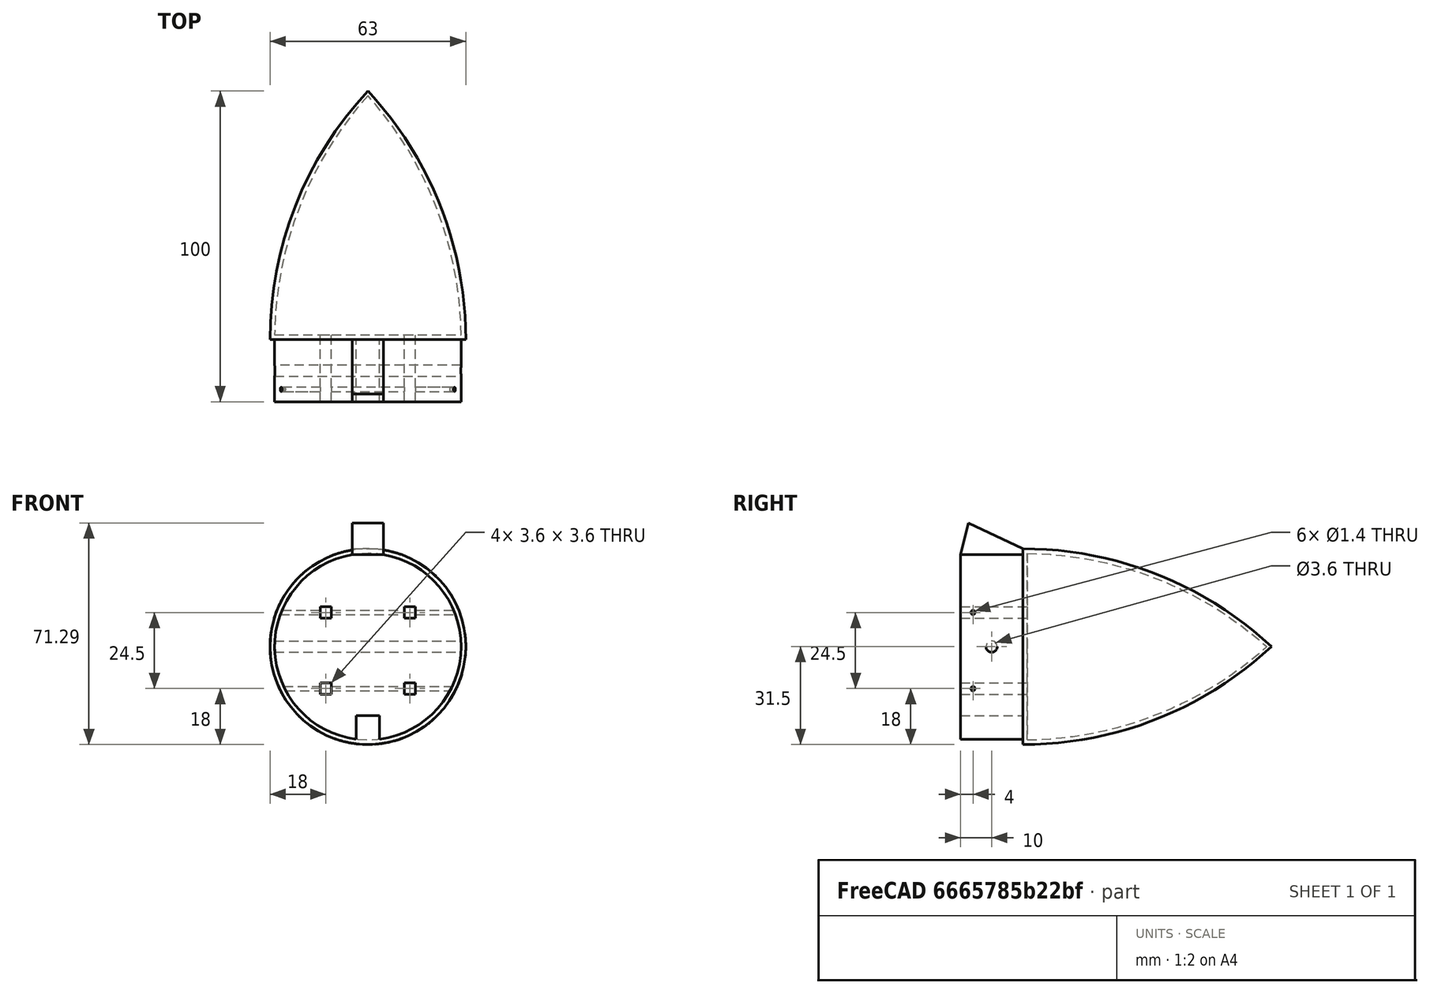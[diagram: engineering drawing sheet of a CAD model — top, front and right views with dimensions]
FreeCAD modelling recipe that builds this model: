
FCSTD DOCUMENT  (FreeCAD 1.0R38641 +468 (Git))
Label: ogive_cam-63_II
License: All rights reserved
LicenseURL: https://en.wikipedia.org/wiki/All_rights_reserved
objects: Sketcher::SketchObject×9, PartDesign::Pocket×6, PartDesign::Pad×2, PartDesign::Revolution×1, PartDesign::Mirrored×1, PartDesign::Body×1, Mesh::Feature×1
note: 48 computed .brp shape members not serialized (recipe doc carries the construction recipe); baked Part::Feature solids carry a one-line shape summary decoded from their .brp

FEATURE [Sketcher::SketchObject] Sketch
  ArcFitTolerance = 1e-06
  AttachmentSupport = -> [XY_Plane]
  FullyConstrained = false
  MakeInternals = false
  MapMode = 5
  sketch-geometry (6):
    g0: ArcOfCircle CenterX=85.695 CenterY=0.0560175 CenterZ=0 NormalX=0 NormalY=0 NormalZ=1 AngleXU=0 Radius=117.195 StartAngle=2.3909 EndAngle=3.14207
    g1: ArcOfCircle CenterX=87.6667 CenterY=0 CenterZ=0 NormalX=0 NormalY=0 NormalZ=1 AngleXU=0 Radius=117.676 StartAngle=2.4113 EndAngle=3.12885
    g2: LineSegment StartX=-1.42e-14 StartY=78.5 StartZ=0 EndX=1.42e-14 EndY=80 EndZ=0
    g3: LineSegment StartX=-30 StartY=1.5 StartZ=0 EndX=0 EndY=1.5 EndZ=0
    g4: LineSegment StartX=0 StartY=1.5 StartZ=0 EndX=0 EndY=0 EndZ=0
    g5: LineSegment StartX=0 StartY=0 StartZ=0 EndX=-31.5 EndY=0 EndZ=0
  constraints (18):
    c: PointOnObject(g0,g-2)
    c: DistanceY(g-1,g0) = 80
    c: PointOnObject(g1,g-1)
    c: PointOnObject(g1,g-2)
    c: Coincident(g2,g1)
    c: Coincident(g2,g0)
    c: Coincident(g1,g3)
    c: Coincident(g3,g4)
    c: Coincident(g4,g-1)
    c: Vertical(g4)
    c: Coincident(g4,g5)
    c: Coincident(g5,g0)
    c: Horizontal(g5)
    c: DistanceY(g2,g2) = 1.5
    c: DistanceY(g4,g4) = 1.5
    c: DistanceY(g4,g1) = 1.5
    c: DistanceX(g0,g1) = 1.5
    c: DistanceX(g0,g4) = 31.5
FEATURE [PartDesign::Revolution] Revolution
  Angle = 360
  Angle2 = 60
  Axis = (0,1,0)
  Base = (0,0,0)
  Profile = -> Sketch
  ReferenceAxis = -> Sketch [V_Axis]
  Refine = true
  Suppressed = false
  Type = 0
FEATURE [Sketcher::SketchObject] Sketch001
  ArcFitTolerance = 1e-06
  AttachmentSupport = -> [Revolution]
  FullyConstrained = true
  MakeInternals = false
  MapMode = 5
  Placement = pos=(0,0,0) rot=(1,0,0;1.5708rad)
  sketch-geometry (1):
    g0: Circle CenterX=0 CenterY=0 CenterZ=0 NormalX=0 NormalY=0 NormalZ=1 AngleXU=0 Radius=30
  constraints (2):
    c: Diameter(g0) = 60
    c: Coincident(g0,g-1)
FEATURE [PartDesign::Pad] Pad
  BaseFeature = -> Revolution
  Direction = (0,-1,2e-16)
  Length = 20
  Length2 = 10
  Profile = -> Sketch001
  ReferenceAxis = -> Sketch001 [N_Axis]
  Suppressed = false
  Type = 0
FEATURE [Sketcher::SketchObject] Sketch002
  ArcFitTolerance = 1e-06
  AttachmentSupport = -> [Pad]
  FullyConstrained = true
  MakeInternals = false
  MapMode = 5
  Placement = pos=(0,-20,4.4e-15) rot=(1,0,0;1.5708rad)
  sketch-geometry (4):
    g0: LineSegment StartX=-5 StartY=29 StartZ=0 EndX=5 EndY=29 EndZ=0
    g1: LineSegment StartX=5 StartY=29 StartZ=0 EndX=5 EndY=41 EndZ=0
    g2: LineSegment StartX=5 StartY=41 StartZ=0 EndX=-5 EndY=41 EndZ=0
    g3: LineSegment StartX=-5 StartY=41 StartZ=0 EndX=-5 EndY=29 EndZ=0
  constraints (11):
    c: Coincident(g0,g1)
    c: Coincident(g1,g2)
    c: Coincident(g2,g3)
    c: Coincident(g3,g0)
    c: Horizontal(g2)
    c: Vertical(g1)
    c: Vertical(g3)
    c: Distance(g1,g3) = 10
    c: Distance(g0,g2) = 12
    c: DistanceY(g-1,g0) = 29
    c: Symmetric(g0,g0,g-2)
FEATURE [PartDesign::Pad] Pad001
  BaseFeature = -> Pad
  Direction = (0,-1,2e-16)
  Length = 20
  Length2 = 10
  Profile = -> Sketch002
  ReferenceAxis = -> Sketch002 [N_Axis]
  Reversed = true
  Suppressed = false
  Type = 0
FEATURE [Sketcher::SketchObject] Sketch003
  ArcFitTolerance = 1e-06
  AttachmentSupport = -> [Pad001]
  ExternalGeometry = -> [Pad001]
  FullyConstrained = true
  MakeInternals = false
  MapMode = 5
  Placement = pos=(-5,0,0) rot=(0.57735,-0.57735,-0.57735;2.0944rad)
  sketch-geometry (3):
    g0: LineSegment StartX=20 StartY=41 StartZ=0 EndX=0 EndY=31.5 EndZ=0
    g1: LineSegment StartX=0 StartY=31.5 StartZ=0 EndX=0 EndY=41 EndZ=0
    g2: LineSegment StartX=0 StartY=41 StartZ=0 EndX=20 EndY=41 EndZ=0
  constraints (7):
    c: Coincident(g-4,g0)
    c: PointOnObject(g0,g-2)
    c: Coincident(g0,g1)
    c: Coincident(g1,g-4)
    c: Coincident(g1,g2)
    c: Coincident(g2,g0)
    c: DistanceY(g-1,g0) = 31.5
FEATURE [PartDesign::Pocket] Pocket
  BaseFeature = -> Pad001
  Direction = (1,0,0)
  Length = 5
  Length2 = 5
  Profile = -> Sketch003
  ReferenceAxis = -> Sketch003 [N_Axis]
  Suppressed = false
  Type = 1
FEATURE [Sketcher::SketchObject] Sketch004
  ArcFitTolerance = 1e-06
  AttachmentSupport = -> [Pocket]
  ExternalGeometry = -> [Pocket]
  FullyConstrained = false
  MakeInternals = false
  MapMode = 5
  Placement = pos=(-5,0,0) rot=(0.57735,-0.57735,-0.57735;2.0944rad)
  sketch-geometry (3):
    g0: LineSegment StartX=20 StartY=29.5804 StartZ=0 EndX=17.3381 EndY=40.211 EndZ=0
    g1: LineSegment StartX=17.3381 StartY=40.211 StartZ=0 EndX=20 EndY=41 EndZ=0
    g2: LineSegment StartX=20 StartY=41 StartZ=0 EndX=20 EndY=29.5804 EndZ=0
  constraints (5):
    c: Coincident(g-3,g0)
    c: Coincident(g0,g1)
    c: Coincident(g1,g-3)
    c: Coincident(g1,g2)
    c: Coincident(g2,g0)
FEATURE [PartDesign::Pocket] Pocket001
  BaseFeature = -> Pocket
  Direction = (1,0,0)
  Length = 5
  Length2 = 5
  Profile = -> Sketch004
  ReferenceAxis = -> Sketch004 [N_Axis]
  Suppressed = false
  Type = 1
FEATURE [Sketcher::SketchObject] Sketch005
  ArcFitTolerance = 1e-06
  AttachmentSupport = -> [Pocket001]
  FullyConstrained = true
  MakeInternals = false
  MapMode = 5
  Placement = pos=(0,-20,4.4e-15) rot=(1,0,0;1.5708rad)
  sketch-geometry (4):
    g0: LineSegment StartX=-3.7 StartY=-22.2 StartZ=0 EndX=-3.7 EndY=-30.2 EndZ=0
    g1: LineSegment StartX=-3.7 StartY=-30.2 StartZ=0 EndX=3.7 EndY=-30.2 EndZ=0
    g2: LineSegment StartX=3.7 StartY=-30.2 StartZ=0 EndX=3.7 EndY=-22.2 EndZ=0
    g3: LineSegment StartX=3.7 StartY=-22.2 StartZ=0 EndX=-3.7 EndY=-22.2 EndZ=0
  constraints (11):
    c: Coincident(g0,g1)
    c: Coincident(g1,g2)
    c: Coincident(g2,g3)
    c: Coincident(g3,g0)
    c: Vertical(g0)
    c: Vertical(g2)
    c: Horizontal(g1)
    c: DistanceY(g0,g0) = 8
    c: DistanceY(g0,g-1) = 22.2
    c: DistanceX(g3,g3) = 7.4
    c: Symmetric(g0,g2,g-2)
FEATURE [PartDesign::Pocket] Pocket002
  BaseFeature = -> Pocket001
  Direction = (0,1,-2e-16)
  Length = 20
  Length2 = 5
  Profile = -> Sketch005
  ReferenceAxis = -> Sketch005 [N_Axis]
  Suppressed = false
  Type = 0
FEATURE [Sketcher::SketchObject] Sketch006
  ArcFitTolerance = 1e-06
  AttachmentSupport = -> [Pocket002]
  FullyConstrained = true
  MakeInternals = false
  MapMode = 5
  Placement = pos=(0,-20,4.4e-15) rot=(1,0,0;1.5708rad)
  sketch-geometry (8):
    g0: LineSegment StartX=-15.3 StartY=12.8 StartZ=0 EndX=-15.3 EndY=9.2 EndZ=0
    g1: LineSegment StartX=-15.3 StartY=9.2 StartZ=0 EndX=-11.7 EndY=9.2 EndZ=0
    g2: LineSegment StartX=-11.7 StartY=9.2 StartZ=0 EndX=-11.7 EndY=12.8 EndZ=0
    g3: LineSegment StartX=-11.7 StartY=12.8 StartZ=0 EndX=-15.3 EndY=12.8 EndZ=0
    g4: LineSegment StartX=-15.3 StartY=-11.7 StartZ=0 EndX=-15.3 EndY=-15.3 EndZ=0
    g5: LineSegment StartX=-15.3 StartY=-15.3 StartZ=0 EndX=-11.7 EndY=-15.3 EndZ=0
    g6: LineSegment StartX=-11.7 StartY=-15.3 StartZ=0 EndX=-11.7 EndY=-11.7 EndZ=0
    g7: LineSegment StartX=-11.7 StartY=-11.7 StartZ=0 EndX=-15.3 EndY=-11.7 EndZ=0
  constraints (24):
    c: Coincident(g0,g1)
    c: Coincident(g1,g2)
    c: Coincident(g2,g3)
    c: Coincident(g3,g0)
    c: Vertical(g0)
    c: Vertical(g2)
    c: Horizontal(g1)
    c: Horizontal(g3)
    c: Distance(g0,g2) = 3.6
    c: Distance(g1,g3) = 3.6
    c: DistanceX(g1,g-1) = 11.7
    c: DistanceY(g-1,g1) = 9.2
    c: Coincident(g4,g5)
    c: Coincident(g5,g6)
    c: Coincident(g6,g7)
    c: Coincident(g7,g4)
    c: Vertical(g4)
    c: Vertical(g6)
    c: Horizontal(g5)
    c: Horizontal(g7)
    c: Distance(g4,g6) = 3.6
    c: Distance(g5,g7) = 3.6
    c: DistanceX(g6,g-1) = 11.7
    c: DistanceY(g6,g-1) = 11.7
FEATURE [PartDesign::Pocket] Pocket003
  BaseFeature = -> Pocket002
  Direction = (0,1,-2e-16)
  Length = 22
  Length2 = 5
  Profile = -> Sketch006
  ReferenceAxis = -> Sketch006 [N_Axis]
  Suppressed = false
  Type = 0
FEATURE [Sketcher::SketchObject] Sketch007
  ArcFitTolerance = 1e-06
  AttachmentSupport = -> [YZ_Plane]
  FullyConstrained = true
  MakeInternals = false
  MapMode = 5
  Placement = pos=(0,0,0) rot=(0.57735,0.57735,0.57735;2.0944rad)
  sketch-geometry (2):
    g0: Circle CenterX=-16 CenterY=-13.5 CenterZ=0 NormalX=0 NormalY=0 NormalZ=1 AngleXU=0 Radius=0.7
    g1: Circle CenterX=-16 CenterY=11 CenterZ=0 NormalX=0 NormalY=0 NormalZ=1 AngleXU=0 Radius=0.7
  constraints (6):
    c: Diameter(g0) = 1.4
    c: DistanceX(g0,g-1) = 16
    c: DistanceY(g0,g-1) = 13.5
    c: Diameter(g1) = 1.4
    c: DistanceX(g1,g-1) = 16
    c: DistanceY(g-1,g1) = 11
FEATURE [PartDesign::Pocket] Pocket004
  BaseFeature = -> Pocket003
  Direction = (-1,0,0)
  Length = 5
  Length2 = 5
  Midplane = true
  Profile = -> Sketch007
  ReferenceAxis = -> Sketch007 [N_Axis]
  Suppressed = false
  Type = 1
FEATURE [Sketcher::SketchObject] Sketch008
  ArcFitTolerance = 1e-06
  AttachmentSupport = -> [YZ_Plane]
  FullyConstrained = true
  MakeInternals = false
  MapMode = 5
  Placement = pos=(0,0,0) rot=(0.57735,0.57735,0.57735;2.0944rad)
  sketch-geometry (1):
    g0: Circle CenterX=-10 CenterY=0 CenterZ=0 NormalX=0 NormalY=0 NormalZ=1 AngleXU=0 Radius=1.8
  constraints (3):
    c: Diameter(g0) = 3.6
    c: PointOnObject(g0,g-1)
    c: DistanceX(g0,g-1) = 10
FEATURE [PartDesign::Pocket] Pocket005
  BaseFeature = -> Pocket004
  Direction = (-1,0,0)
  Length = 5
  Length2 = 5
  Midplane = true
  Profile = -> Sketch008
  ReferenceAxis = -> Sketch008 [N_Axis]
  Suppressed = false
  Type = 1
FEATURE [PartDesign::Mirrored] Mirrored001
  BaseFeature = -> Pocket005
  MirrorPlane = -> Sketch006 [V_Axis]
  Originals = -> [Pocket003]
  Suppressed = false
  TransformMode = 0
FEATURE [PartDesign::Body] Body  label="Corps"
  AllowCompound = false
  Group = -> [Sketch,Revolution,Sketch001,Pad,Sketch002,Pad001,Sketch003,Pocket,Sketch004,Pocket001,Sketch005,Pocket002,Sketch006,Pocket003,Sketch007,Pocket004,Sketch008,Pocket005,Mirrored001]
  Origin = -> Origin
  Tip = -> Mirrored001
FEATURE [Mesh::Feature] Mesh  label="Mirrored001 (Meshed)"
